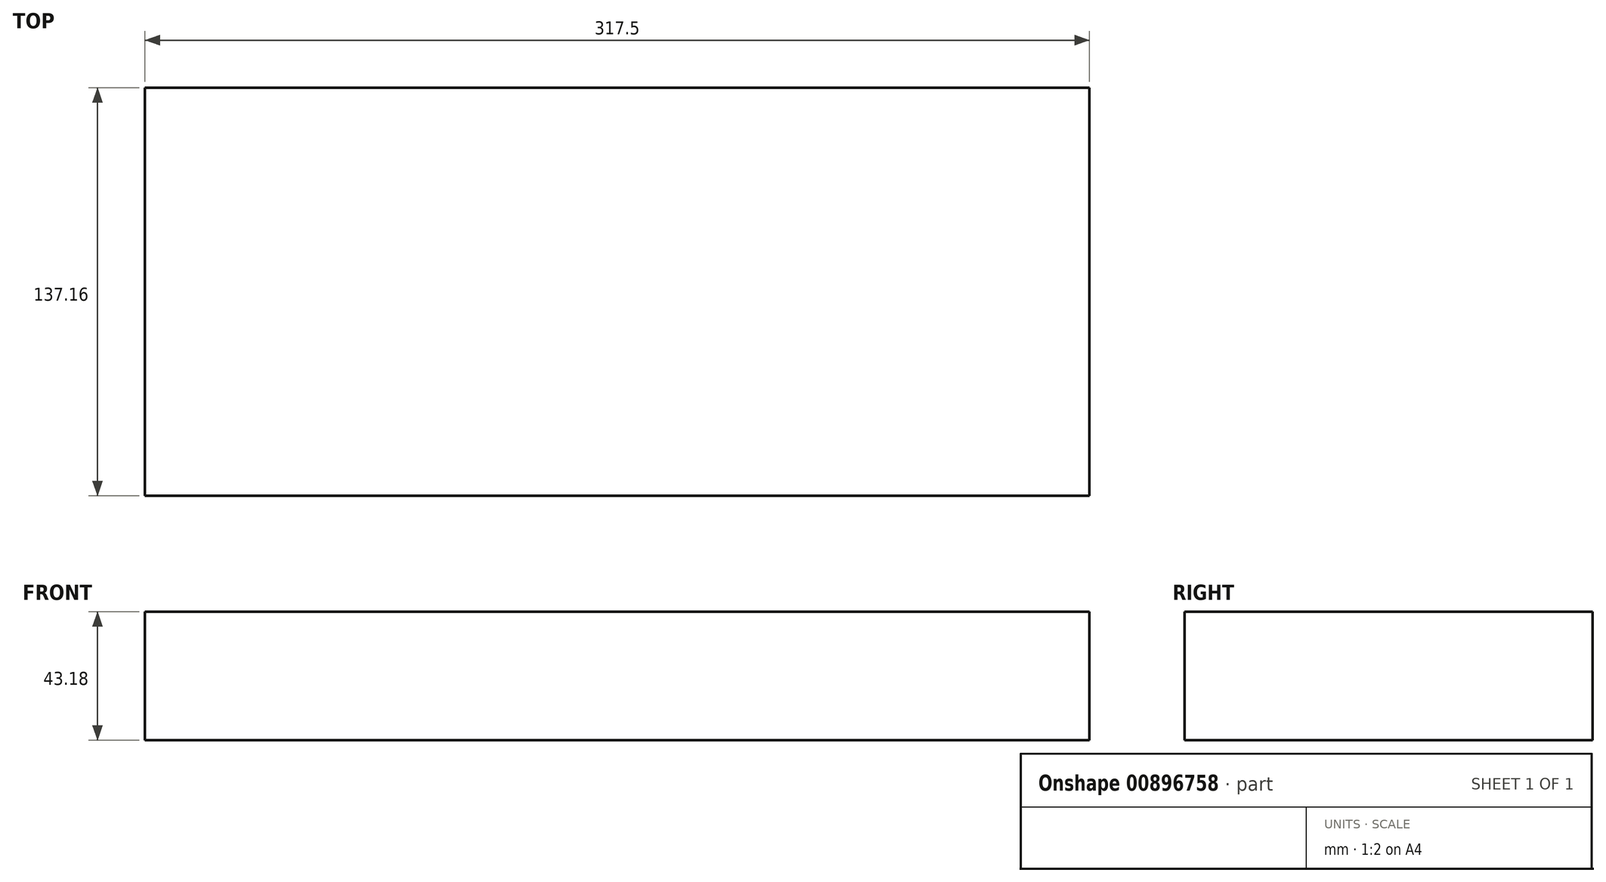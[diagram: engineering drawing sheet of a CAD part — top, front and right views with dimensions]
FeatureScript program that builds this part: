
annotation { "Feature Type Name" : "Feature", "Feature Type Description" : "" }
export const myFeature = defineFeature(function(context is Context, id is Id, definition is map)
    precondition{}
    {
        {
            var Q0;
            Q0=qCreatedBy(makeId("Top.planeOp"),FACE);
            var sketch = newSketch(context, id + "F0", { "sketchPlane" : qUnion([Q0])});
            skLineSegment(sketch, "E0.bottom", {"start": v(0, 0) * mm, "end": v(317.5, 0) * mm});
            skLineSegment(sketch, "E0.top", {"start": v(0, 137.16) * mm, "end": v(317.5, 137.16) * mm});
            skLineSegment(sketch, "E0.left", {"start": v(0, 0) * mm, "end": v(0, 137.16) * mm});
            skLineSegment(sketch, "E0.right", {"start": v(317.5, 0) * mm, "end": v(317.5, 137.16) * mm});
            skSolve(sketch);
        }
        {
            var Q0;
            Q0=makeQuery(id+"F0.imprint","IMPRINT",FACE,{"disambiguationData":[TD([[makeQuery(id+"F0.imprint","IMPRINT",EDGE,{"derivedFrom":sQuery(id+"F0.wireOp",EDGE,"E0.bottom")}),1.0]])]});
            extrude(context, id + "F1", {"entities" : qUnion([Q0]), "depth" : 43.18 * mm, "offsetDistance" : 25.4 * mm});
        }
        {
            var Q0;
            Q0=makeQuery(id+"F1.opExtrude","SWEPT_FACE",FACE,{"disambiguationData":[OSD([sQuery(id+"F0.wireOp",EDGE,"E0.top")])]});
            var sketch = newSketch(context, id + "F2", { "sketchPlane" : qUnion([Q0])});
            skCircle(sketch, "E1", {"center": v(-88.9, 25.4) * mm, "radius": 3.81 * mm});
            skSolve(sketch);
        }
    });
